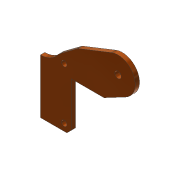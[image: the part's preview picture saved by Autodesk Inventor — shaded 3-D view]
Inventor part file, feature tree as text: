
AUTODESK INVENTOR PART (.ipt)
format: ipt  version: 2019.4 (Build 234330000, 330)  size: 108,032 bytes
history: native  units: mm
features: other x6, reference x6, hole x2, sketch x1, extrude x1
ambient origin geometry x8: Origin, YZ Plane, XZ Plane, XY Plane, X Axis, Y Axis, Z Axis, Center Point
bodies: Body1 (feature_tree)
feature tree (16):
  other  "ソリッド1"
  sketch  "スケッチ1"
  extrude  "押し出し1"  Depth=10.0mm
  hole  "穴1"  [1 undecoded]
  hole  "穴2"  [1 undecoded]
  reference  "参照1"
  reference  "参照2"
  reference  "参照3"
  reference  "参照4"
  reference  "参照5"
  reference  "参照6"
  parser-record x1  (decoder bookkeeping rows leaked as tree rows — omitted from the tree; the rows remain in map.json)
  other  "HIP_UNIT.iam"
  other  "XM430_ASM_WITHOUT-BACK:1"
  other  "XM430_HORN:1"
  other  "XM430_HOUSING_TOP:1"
note: 2 required parameter values undecoded (feature->parameter linkage not recoverable at this tier; creation-order binding heuristic only, values carry confidence <= 0.55)
note: 1 file-system path scrubbed to <path> (originals preserved in map.json)
